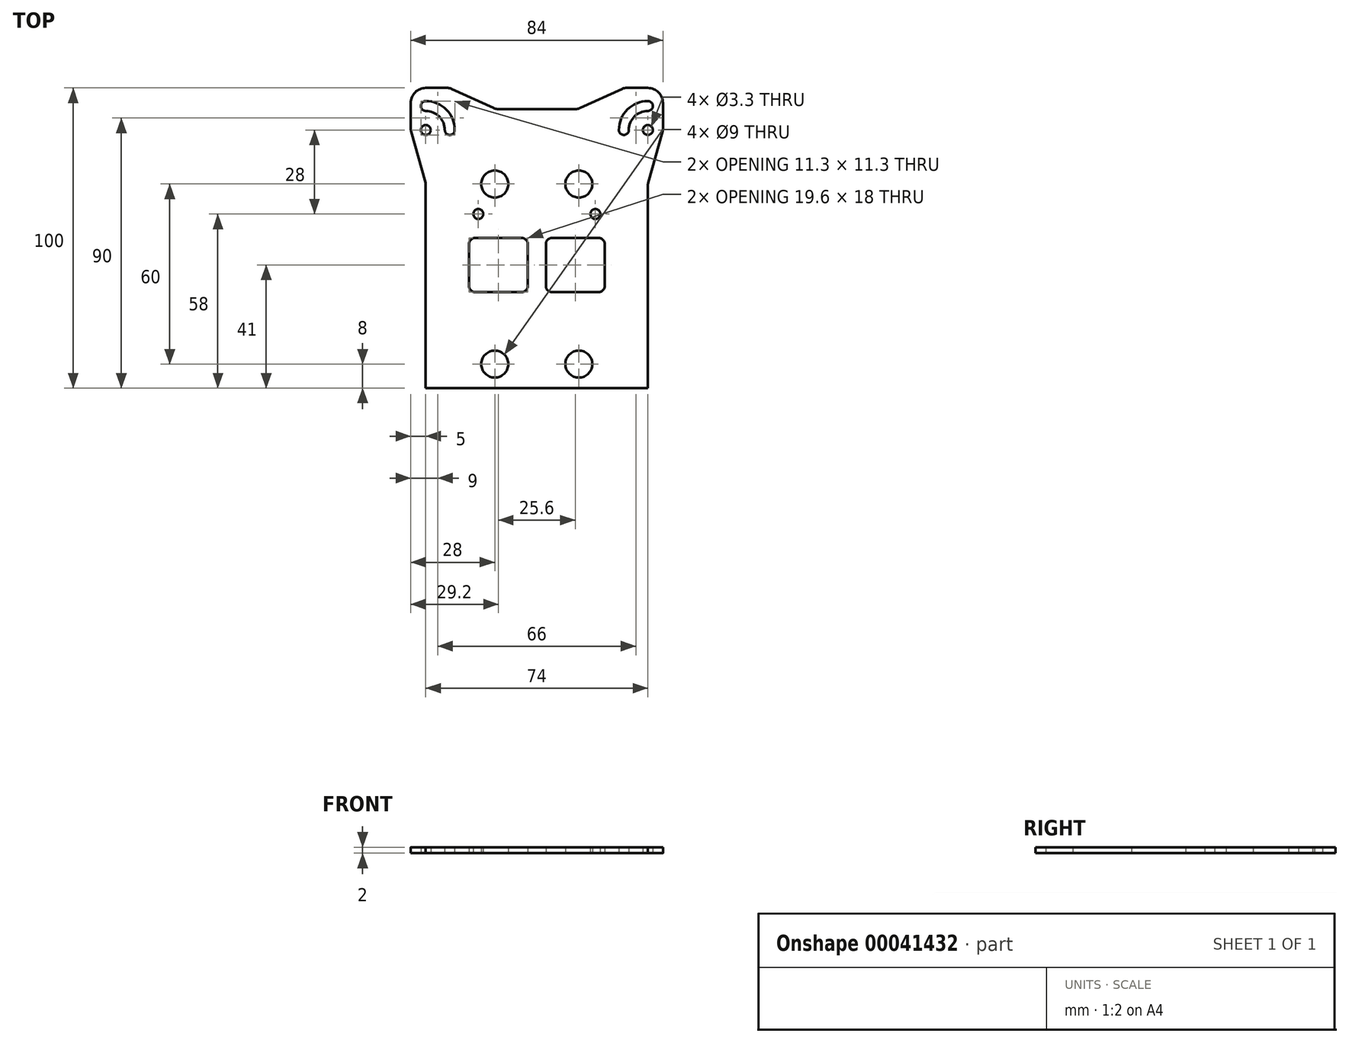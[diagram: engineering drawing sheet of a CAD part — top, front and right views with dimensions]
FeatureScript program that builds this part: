
annotation { "Feature Type Name" : "Feature", "Feature Type Description" : "" }
export const myFeature = defineFeature(function(context is Context, id is Id, definition is map)
    precondition{}
    {
        {
            var Q0;
            Q0=qCreatedBy(makeId("Top.planeOp"),FACE);
            var sketch = newSketch(context, id + "F0", { "sketchPlane" : qUnion([Q0])});
            skLineSegment(sketch, "E0", {"start": v(0, 75.22) * mm, "end": v(0, -74.72) * mm, "construction": true});
            skLineSegment(sketch, "E1.0", {"start": v(-37, 75.22) * mm, "end": v(-37, -74.72) * mm, "construction": true});
            skLineSegment(sketch, "E2.0", {"start": v(37, 75.22) * mm, "end": v(37, -74.72) * mm, "construction": true});
            skLineSegment(sketch, "E3", {"start": v(-37, 60.22) * mm, "end": v(-29.66, 60.22) * mm});
            skLineSegment(sketch, "E4.0", {"start": v(-37.5, 28.22) * mm, "end": v(37.5, 28.22) * mm, "construction": true});
            skLineSegment(sketch, "E5.0", {"start": v(-42, 46.22) * mm, "end": v(37.5, 46.22) * mm, "construction": true});
            skCircle(sketch, "E6", {"center": v(-37, 46.22) * mm, "radius": 1.65 * mm});
            skLineSegment(sketch, "E7.0", {"start": v(-29, 60.22) * mm, "end": v(-29, -74.72) * mm, "construction": true});
            skArc(sketch, "E8", {"start": v(-29, 46.22) * mm, "mid": v(-31.34, 51.88) * mm, "end": v(-37, 54.22) * mm, "construction": true});
            skArc(sketch, "E9.0", {"start": v(-27.35, 46.22) * mm, "mid": v(-30.18, 53.04) * mm, "end": v(-37, 55.87) * mm});
            skArc(sketch, "E10.0", {"start": v(-30.65, 46.22) * mm, "mid": v(-32.5, 50.7) * mm, "end": v(-37, 52.57) * mm});
            skArc(sketch, "E11", {"start": v(-37, 55.87) * mm, "mid": v(-38.65, 54.22) * mm, "end": v(-37, 52.57) * mm});
            skArc(sketch, "E12", {"start": v(-27.35, 46.22) * mm, "mid": v(-29, 44.57) * mm, "end": v(-30.65, 46.22) * mm});
            skLineSegment(sketch, "E13", {"start": v(-41.9, 45.83) * mm, "end": v(-37.1, 28.61) * mm});
            skLineSegment(sketch, "E14", {"start": v(-37, 27.81) * mm, "end": v(-37, -39.78) * mm});
            skLineSegment(sketch, "E15", {"start": v(-42, 55.22) * mm, "end": v(-42, 46.63) * mm});
            skPoint(sketch, "E16.visualSharp", {"position": v(-42, 60.22) * mm});
            skArc(sketch, "E16.filletArc", {"start": v(-37, 60.22) * mm, "mid": v(-40.54, 58.76) * mm, "end": v(-42, 55.22) * mm});
            skPoint(sketch, "E17.visualSharp", {"position": v(-42, 46.22) * mm});
            skArc(sketch, "E17.filletArc", {"start": v(-42, 46.63) * mm, "mid": v(-41.97, 46.22) * mm, "end": v(-41.9, 45.83) * mm});
            skPoint(sketch, "E18.visualSharp", {"position": v(-37, 28.22) * mm});
            skArc(sketch, "E18.filletArc", {"start": v(-37, 27.81) * mm, "mid": v(-37.03, 28.22) * mm, "end": v(-37.1, 28.61) * mm});
            skLineSegment(sketch, "E19.0", {"start": v(-37, 53.22) * mm, "end": v(-32.5, 53.22) * mm});
            skLineSegment(sketch, "E20.0", {"start": v(-13.75, 60.22) * mm, "end": v(-13.75, -89.72) * mm, "construction": true});
            skLineSegment(sketch, "E21", {"start": v(-28.4, 59.95) * mm, "end": v(-14.35, 53.5) * mm});
            skLineSegment(sketch, "E22.trimOffspring", {"start": v(-13.1, 53.22) * mm, "end": v(0, 53.22) * mm});
            skPoint(sketch, "E23.visualSharp", {"position": v(-13.75, 53.22) * mm});
            skArc(sketch, "E23.filletArc", {"start": v(-14.35, 53.5) * mm, "mid": v(-13.73, 53.29) * mm, "end": v(-13.1, 53.22) * mm});
            skPoint(sketch, "E24.visualSharp", {"position": v(-29, 60.22) * mm});
            skArc(sketch, "E24.filletArc", {"start": v(-28.4, 59.95) * mm, "mid": v(-29.02, 60.15) * mm, "end": v(-29.66, 60.22) * mm});
            skLineSegment(sketch, "E25.trimOffspring", {"start": v(-37, -39.78) * mm, "end": v(37, -39.78) * mm});
            skPoint(sketch, "E26.orphan", {"position": v(-37.5, -39.78) * mm});
            skLineSegment(sketch, "E27.MirrorCS", {"start": v(-3, 8.22) * mm, "end": v(-3, -5.78) * mm});
            skLineSegment(sketch, "E28.MirrorCS", {"start": v(3, 8.22) * mm, "end": v(3, -5.78) * mm});
            skLineSegment(sketch, "E29.MirrorCS", {"start": v(-22.6, 8.22) * mm, "end": v(-22.6, -5.78) * mm});
            skCircle(sketch, "E30.MirrorC", {"center": v(37, 46.22) * mm, "radius": 1.65 * mm});
            skArc(sketch, "E31.MirrorCS", {"start": v(42, 46.63) * mm, "mid": v(41.97, 46.22) * mm, "end": v(41.9, 45.83) * mm});
            skArc(sketch, "E32.MirrorCS", {"start": v(27.35, 46.22) * mm, "mid": v(29, 44.57) * mm, "end": v(30.65, 46.22) * mm});
            skArc(sketch, "E33.MirrorCS", {"start": v(37, 27.81) * mm, "mid": v(37.03, 28.22) * mm, "end": v(37.1, 28.61) * mm});
            skArc(sketch, "E34.MirrorCS", {"start": v(14.35, 53.5) * mm, "mid": v(13.73, 53.29) * mm, "end": v(13.1, 53.22) * mm});
            skArc(sketch, "E35.MirrorCS", {"start": v(28.4, 59.95) * mm, "mid": v(29.02, 60.15) * mm, "end": v(29.66, 60.22) * mm});
            skArc(sketch, "E36.MirrorCS", {"start": v(37, 55.87) * mm, "mid": v(38.65, 54.22) * mm, "end": v(37, 52.57) * mm});
            skLineSegment(sketch, "E37.MirrorCS", {"start": v(37, 53.22) * mm, "end": v(32.5, 53.22) * mm});
            skArc(sketch, "E38.MirrorCS", {"start": v(37, 60.22) * mm, "mid": v(40.54, 58.76) * mm, "end": v(42, 55.22) * mm});
            skArc(sketch, "E39.MirrorCS", {"start": v(30.65, 46.22) * mm, "mid": v(32.5, 50.7) * mm, "end": v(37, 52.57) * mm});
            skLineSegment(sketch, "E40.MirrorCS", {"start": v(42, 55.22) * mm, "end": v(42, 46.63) * mm});
            skLineSegment(sketch, "E41.MirrorCS", {"start": v(37, 27.81) * mm, "end": v(37, -39.78) * mm});
            skPoint(sketch, "E42.MirrorP", {"position": v(13.75, 53.22) * mm});
            skLineSegment(sketch, "E43.MirrorCS", {"start": v(28.4, 59.95) * mm, "end": v(14.35, 53.5) * mm});
            skPoint(sketch, "E44.MirrorP", {"position": v(42, 46.22) * mm});
            skArc(sketch, "E45.MirrorCS", {"start": v(29, 46.22) * mm, "mid": v(31.34, 51.88) * mm, "end": v(37, 54.22) * mm, "construction": true});
            skPoint(sketch, "E46.MirrorP", {"position": v(42, 60.22) * mm});
            skLineSegment(sketch, "E47.MirrorCS", {"start": v(37, 60.22) * mm, "end": v(29.66, 60.22) * mm});
            skPoint(sketch, "E48.MirrorP", {"position": v(37, 28.22) * mm});
            skLineSegment(sketch, "E49.MirrorCS", {"start": v(22.6, 8.22) * mm, "end": v(22.6, -5.78) * mm});
            skArc(sketch, "E50.MirrorCS", {"start": v(27.35, 46.22) * mm, "mid": v(30.18, 53.04) * mm, "end": v(37, 55.87) * mm});
            skPoint(sketch, "E51.MirrorP", {"position": v(29, 60.22) * mm});
            skPoint(sketch, "E52.MirrorP", {"position": v(37.5, -39.78) * mm});
            skLineSegment(sketch, "E53.MirrorCS", {"start": v(41.9, 45.83) * mm, "end": v(37.1, 28.61) * mm});
            skLineSegment(sketch, "E54.MirrorCS", {"start": v(13.1, 53.22) * mm, "end": v(0, 53.22) * mm});
            skLineSegment(sketch, "E55.0", {"start": v(-22.6, -31.78) * mm, "end": v(22.6, -31.78) * mm, "construction": true});
            skLineSegment(sketch, "E56.0", {"start": v(-14, 75.22) * mm, "end": v(-14, -74.72) * mm, "construction": true});
            skCircle(sketch, "E57", {"center": v(-14, 28.22) * mm, "radius": 4.5 * mm});
            skCircle(sketch, "E58.MirrorC", {"center": v(14, 28.22) * mm, "radius": 4.5 * mm});
            skLineSegment(sketch, "E59.0", {"start": v(-37.5, 18.22) * mm, "end": v(37.5, 18.22) * mm, "construction": true});
            skLineSegment(sketch, "E60.0", {"start": v(-19.5, 75.22) * mm, "end": v(-19.5, -74.72) * mm, "construction": true});
            skCircle(sketch, "E61", {"center": v(-19.5, 18.22) * mm, "radius": 1.65 * mm});
            skCircle(sketch, "E62.MirrorC", {"center": v(19.5, 18.22) * mm, "radius": 1.65 * mm});
            skCircle(sketch, "E63", {"center": v(-14, -31.78) * mm, "radius": 4.5 * mm});
            skCircle(sketch, "E64.MirrorC", {"center": v(14, -31.78) * mm, "radius": 4.5 * mm});
            skLineSegment(sketch, "E65", {"start": v(-20.6, 10.22) * mm, "end": v(-5, 10.22) * mm});
            skLineSegment(sketch, "E66", {"start": v(-20.6, -7.78) * mm, "end": v(-5, -7.78) * mm});
            skLineSegment(sketch, "E67", {"start": v(5, 10.22) * mm, "end": v(20.6, 10.22) * mm});
            skLineSegment(sketch, "E68", {"start": v(5, -7.78) * mm, "end": v(20.6, -7.78) * mm});
            skPoint(sketch, "E69.orphan", {"position": v(-22.6, 1.22) * mm});
            skPoint(sketch, "E70.orphan", {"position": v(22.6, 1.22) * mm});
            skPoint(sketch, "E71.visualSharp", {"position": v(-22.6, 10.22) * mm});
            skArc(sketch, "E71.filletArc", {"start": v(-20.6, 10.22) * mm, "mid": v(-22.01, 9.63) * mm, "end": v(-22.6, 8.22) * mm});
            skPoint(sketch, "E72.visualSharp", {"position": v(-3, 10.22) * mm});
            skArc(sketch, "E72.filletArc", {"start": v(-3, 8.22) * mm, "mid": v(-3.59, 9.63) * mm, "end": v(-5, 10.22) * mm});
            skPoint(sketch, "E73.visualSharp", {"position": v(-3, -7.78) * mm});
            skArc(sketch, "E73.filletArc", {"start": v(-5, -7.78) * mm, "mid": v(-3.59, -7.2) * mm, "end": v(-3, -5.78) * mm});
            skPoint(sketch, "E74.visualSharp", {"position": v(-22.6, -7.78) * mm});
            skArc(sketch, "E74.filletArc", {"start": v(-22.6, -5.78) * mm, "mid": v(-22.01, -7.2) * mm, "end": v(-20.6, -7.78) * mm});
            skPoint(sketch, "E75.visualSharp", {"position": v(3, 10.22) * mm});
            skArc(sketch, "E75.filletArc", {"start": v(5, 10.22) * mm, "mid": v(3.59, 9.63) * mm, "end": v(3, 8.22) * mm});
            skPoint(sketch, "E76.visualSharp", {"position": v(22.6, 10.22) * mm});
            skArc(sketch, "E76.filletArc", {"start": v(22.6, 8.22) * mm, "mid": v(22.01, 9.63) * mm, "end": v(20.6, 10.22) * mm});
            skPoint(sketch, "E77.visualSharp", {"position": v(22.6, -7.78) * mm});
            skArc(sketch, "E77.filletArc", {"start": v(20.6, -7.78) * mm, "mid": v(22.01, -7.2) * mm, "end": v(22.6, -5.78) * mm});
            skPoint(sketch, "E78.visualSharp", {"position": v(3, -7.78) * mm});
            skArc(sketch, "E78.filletArc", {"start": v(3, -5.78) * mm, "mid": v(3.59, -7.2) * mm, "end": v(5, -7.78) * mm});
            skPoint(sketch, "E79.orphan", {"position": v(-22.6, -39.78) * mm});
            skPoint(sketch, "E80.orphan", {"position": v(22.6, -39.78) * mm});
            skSolve(sketch);
        }
        {
            var Q0;
            Q0=makeQuery(id+"F0.imprint","IMPRINT",FACE,{"disambiguationData":[TD([[makeQuery(id+"F0.imprint","IMPRINT",EDGE,{"derivedFrom":sQuery(id+"F0.wireOp",EDGE,"E3")}),-1.0]])]});
            extrude(context, id + "F1", {"entities" : qUnion([Q0]), "depth" : 2 * mm});
        }
    });
